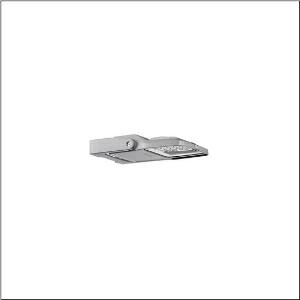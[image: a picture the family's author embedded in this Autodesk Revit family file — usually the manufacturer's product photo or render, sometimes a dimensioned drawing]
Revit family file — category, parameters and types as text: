
# Revit family: floodlight_fl_21_iq_micro___pl43_5xa7761a4a2a_9599
name_source: partatom
category: Lighting Fixtures
units: mm (PartAtom-declared; Revit-internal decimal feet)

## family parameters
Cut with Voids When Loaded = No
Host = Face
Light Source = No
Part Type = Normal
Room Calculation Point = No
Round Connector Dimension = Use Diameter
Shared = No

## types (1)
- --- (1 x LED, 3170 lm, 23.1 W, 4000K)
    Apparent Load = 23 VA
    CIE Flux Codes = 29 80 99 100 100
    Color Rendering = 70
    Color Temperature = 4000K
    Default Elevation = 1800 mm
    Description = Floodlight FL 21 iQ micro, floodlight, primary light control with lens, of PMMA, primary optical cover: protective disc, of toughened safety glass, transparent, light distribution: PL43, light emission: direct distribution, installation type: surface-mounted, LED, High Power LED, rated luminous flux: 3.170lm, luminous efficacy: 137lm/W, light colour: 740, colour temperature: 4000K, control: optimised constant luminous flux control (CLO 2.0), Desk-Remote (wireless, voltage-free reading and setting of iQ features in the workshop via application-optimized NFC function/RFID function), Light-Fading, Smart-Wire, Night-Set, Lumen-Switch, Temp-Guard, Auto-Match, with terminal, 6-pole, mains connection: 220..240V, AC, 50/60Hz, start of lifetime: 23W, end of service life: 24W, reduction: 11W, luminaire housing, of diecast aluminium, powder-coated, Siteco® metallic grey (DB 702S), corrosivity category C5 mid according to DIN EN ISO 12944, sealing non-destructively replaceable, design bracket, of diecast aluminium, powder-coated, Siteco® metallic grey (DB 702S), protection rating (complete): IP66, insulation class (complete): insulation class II (safety insulation), certification: CE, ENEC, VDE, protection symbol: D, impact resistance: IK07, permissible operating ambient temperature: -40..+40°C, permissible operating ambient temperature for outdoor applications: -40..+50°C, standard: DIN EN 12944, LABS conformity tested according to VDMA 24364:2018-05, packaging unit: 1 piece

Light Distribution: PL43
    Height = 65 mm
    Lamp = 1 x LED
    Lamp Light Flux = 3170 lm
    Lamp Power = 23.1 W
    Lamp count = 1
    Length = 312 mm
    Luminous efficacy = 137 lm/W
    Manufacturer = Siteco
    ModVariant = No
    Model = 5XA7761A4A2A
    Mounting Place = Wall
    Mounting Type = Surface mounted
    Number of Poles = 1
    OnlyDefault = Yes
    Power Factor = 1
    Product Name = Floodlight FL 21 iQ micro | PL43
    Product group = floodlight | wall mounted
    ProductGroupID = 2001
    Protection Class = Protection class II
    Protection Degree = IP 66
    RLX_Detail_Level = 1
    RLX_Emergency_Light_Flux = 0 lm
    RLX_Emergency_Type = 0
    RLX_Emergency_Type_DB = No
    RlxData = <blob elided: 97221 chars, md5=bb9fe1fb>
    Socket = socket
    Standby Power = 0 W
    System Light Flux = 3170 lm
    System Power = 23 W
    Type Comments = factory setting: luminous flux: 100 % | dim-lin: 254 | 455 mA
    Type Image = l_1006878.jpg
    URL = http://relux.com
    VarID = @adj_148019
    Voltage = 0 V
    Weight = 0.00 kg
    Width = 230 mm

## geometry (parser evidence)
native form markers: Blend x4, Sweep x12
no freeform markers — native parametric forms only
